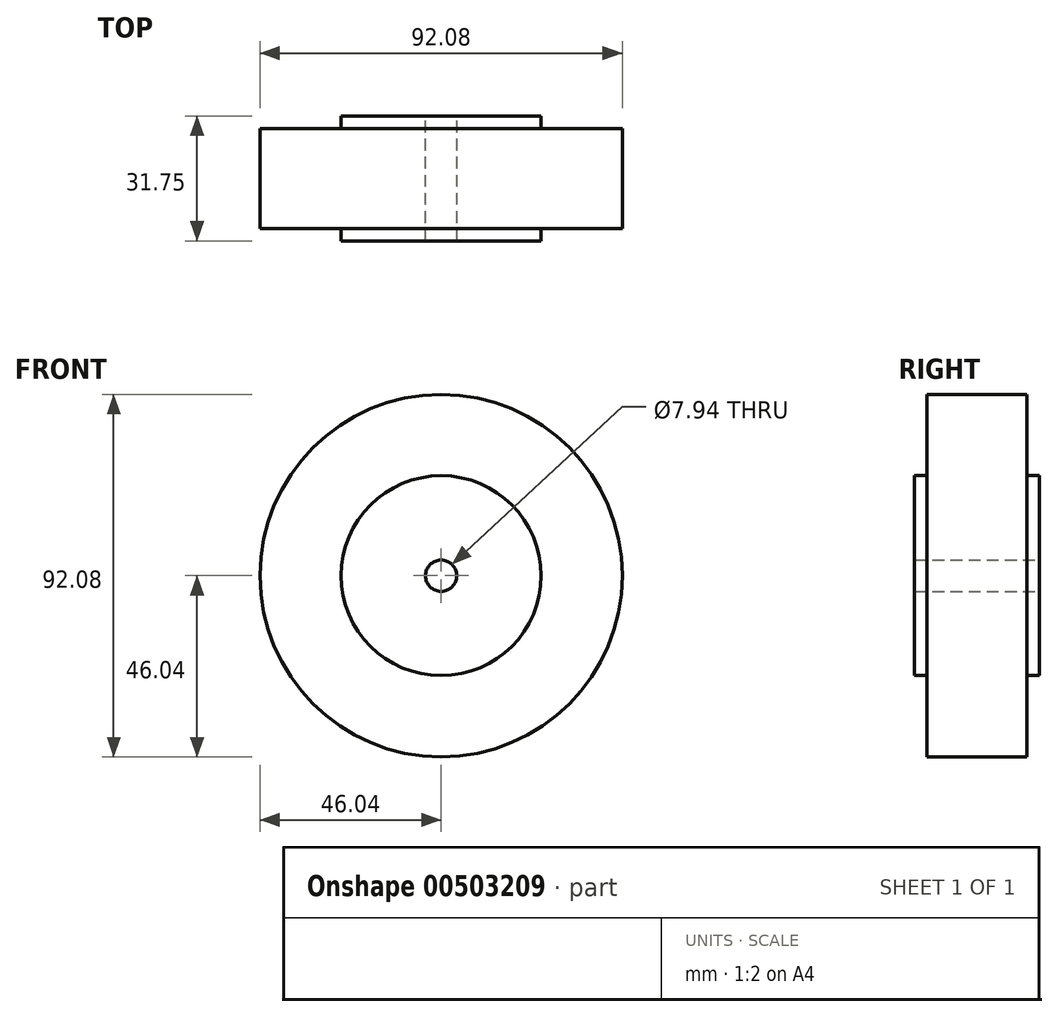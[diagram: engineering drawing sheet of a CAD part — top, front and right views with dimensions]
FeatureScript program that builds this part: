
annotation { "Feature Type Name" : "Feature", "Feature Type Description" : "" }
export const myFeature = defineFeature(function(context is Context, id is Id, definition is map)
    precondition{}
    {
        {
            var Q0;
            Q0=qCreatedBy(makeId("Front.planeOp"),FACE);
            var sketch = newSketch(context, id + "F0", { "sketchPlane" : qUnion([Q0])});
            skCircle(sketch, "E0", {"center": v(0, 0) * mm, "radius": 46.04 * mm});
            skSolve(sketch);
        }
        {
            var Q0;
            Q0=makeQuery(id+"F0.imprint","IMPRINT",FACE,{"disambiguationData":[TD([[makeQuery(id+"F0.imprint","IMPRINT",EDGE,{"derivedFrom":sQuery(id+"F0.wireOp",EDGE,"E0")}),1.0]])]});
            extrude(context, id + "F1", {"entities" : qUnion([Q0]), "depth" : 31.75 * mm});
        }
        {
            var Q0;
            Q0=makeQuery(id+"F1.opExtrude","CAP_FACE",FACE,{"disambiguationData":[OSD([sQuery(id+"F0.wireOp",EDGE,"E0")])],"isStart":false});
            var sketch = newSketch(context, id + "F2", { "sketchPlane" : qUnion([Q0])});
            skCircle(sketch, "E1", {"center": v(0, 0) * mm, "radius": 25.4 * mm});
            skSolve(sketch);
        }
        {
            var Q0;
            Q0=makeQuery(id+"F2.imprint","IMPRINT",FACE,{"disambiguationData":[TD([[makeQuery(id+"F2.imprint","IMPRINT",EDGE,{"derivedFrom":sQuery(id+"F2.wireOp",EDGE,"E1")}),-1.0]])]});
            extrude(context, id + "F3", {"entities" : qUnion([Q0]), "operationType" : NewBodyOperationType.REMOVE, "oppositeDirection" : true, "depth" : 3.17 * mm});
        }
        {
            var Q0;
            Q0=makeQuery(id+"F1.opExtrude","CAP_FACE",FACE,{"disambiguationData":[OSD([sQuery(id+"F0.wireOp",EDGE,"E0")])],"isStart":true});
            var sketch = newSketch(context, id + "F4", { "sketchPlane" : qUnion([Q0])});
            skCircle(sketch, "E2", {"center": v(0, 0) * mm, "radius": 25.4 * mm});
            skSolve(sketch);
        }
        {
            var Q0;
            Q0=makeQuery(id+"F4.imprint","IMPRINT",FACE,{"disambiguationData":[TD([[makeQuery(id+"F4.imprint","IMPRINT",EDGE,{"derivedFrom":sQuery(id+"F4.wireOp",EDGE,"E2")}),-1.0]])]});
            extrude(context, id + "F5", {"entities" : qUnion([Q0]), "operationType" : NewBodyOperationType.REMOVE, "oppositeDirection" : true, "depth" : 3.17 * mm});
        }
        {
            var Q0;
            Q0=qCreatedBy(makeId("Front.planeOp"),FACE);
            var sketch = newSketch(context, id + "F6", { "sketchPlane" : qUnion([Q0])});
            skCircle(sketch, "E3", {"center": v(0, 0) * mm, "radius": 3.97 * mm});
            skSolve(sketch);
        }
        {
            var Q0;
            Q0 = qSketchRegion(id + "F6", true);
            extrude(context, id + "F7", {"entities" : qUnion([Q0]), "operationType" : NewBodyOperationType.REMOVE, "endBound" : BoundingType.THROUGH_ALL, "depth" : 25.4 * mm});
        }
    });
